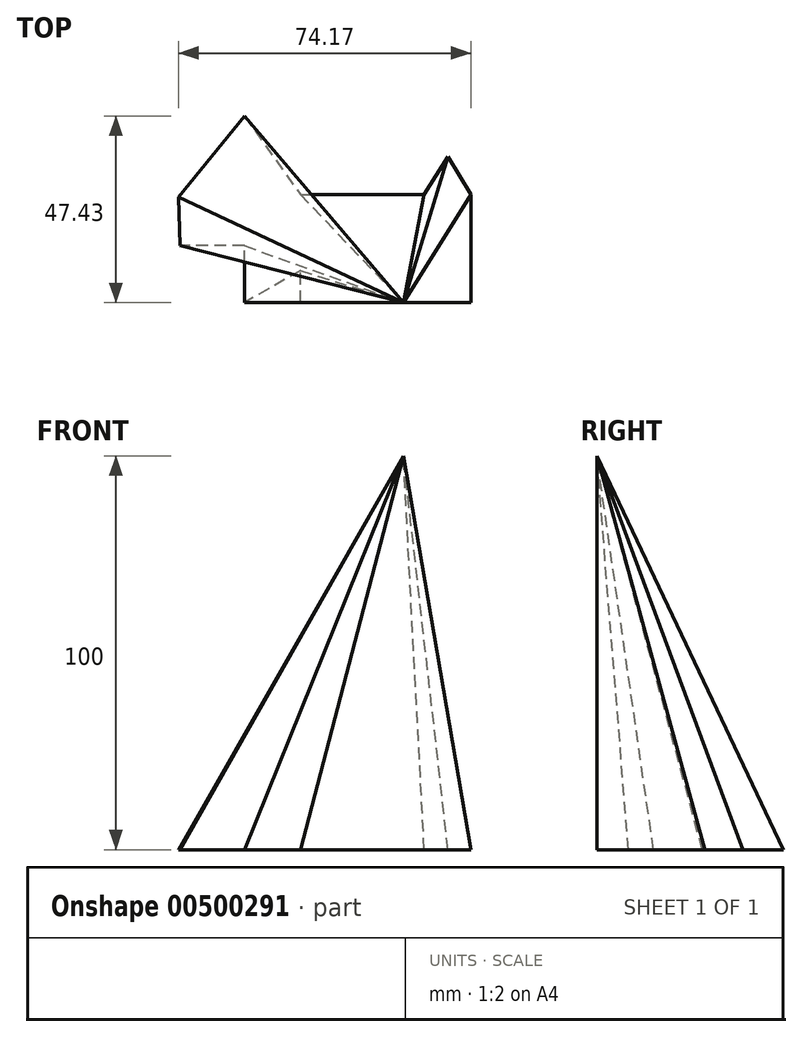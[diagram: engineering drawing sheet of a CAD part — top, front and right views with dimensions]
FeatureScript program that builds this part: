
annotation { "Feature Type Name" : "Feature", "Feature Type Description" : "" }
export const myFeature = defineFeature(function(context is Context, id is Id, definition is map)
    precondition{}
    {
        {
            var Q0;
            Q0=qCreatedBy(makeId("Top.planeOp"),FACE);
            var sketch = newSketch(context, id + "F0", { "sketchPlane" : qUnion([Q0])});
            skLineSegment(sketch, "E0", {"start": v(-57.04, 26.84) * mm, "end": v(-40.4, 47.43) * mm});
            skLineSegment(sketch, "E1", {"start": v(-40.4, 47.43) * mm, "end": v(-26.17, 27.45) * mm});
            skLineSegment(sketch, "E2", {"start": v(-26.17, 27.45) * mm, "end": v(5.32, 27.45) * mm});
            skLineSegment(sketch, "E3", {"start": v(5.32, 27.45) * mm, "end": v(11.37, 37.14) * mm});
            skLineSegment(sketch, "E4", {"start": v(11.37, 37.14) * mm, "end": v(17.13, 27.45) * mm});
            skLineSegment(sketch, "E5", {"start": v(17.13, 27.45) * mm, "end": v(17.13, 0) * mm});
            skLineSegment(sketch, "E6", {"start": v(17.13, 0) * mm, "end": v(-26.17, 0) * mm});
            skLineSegment(sketch, "E7", {"start": v(-26.17, 0) * mm, "end": v(-26.17, 8.07) * mm});
            skLineSegment(sketch, "E8", {"start": v(-26.17, 8.07) * mm, "end": v(-40.4, 0) * mm});
            skLineSegment(sketch, "E9", {"start": v(-40.4, 0) * mm, "end": v(-40.4, 14.43) * mm});
            skLineSegment(sketch, "E10", {"start": v(-40.4, 14.43) * mm, "end": v(-56.74, 14.43) * mm});
            skLineSegment(sketch, "E11", {"start": v(-56.74, 14.43) * mm, "end": v(-57.04, 26.84) * mm});
            skSolve(sketch);
        }
        {
            var Q0;
            Q0=qCreatedBy(makeId("Top.planeOp"),FACE);
            cPlane(context, id + "F1", {"entities" : qUnion([Q0]), "cplaneType" : CPlaneType.OFFSET, "offset" : 100 * mm, "width" : 152.4 * mm, "height" : 152.4 * mm});
        }
        {
            var Q0;
            Q0=qCreatedBy(id+"F1.planeOp",FACE);
            var sketch = newSketch(context, id + "F2", { "sketchPlane" : qUnion([Q0])});
            skPoint(sketch, "E12", {"position": v(0, 0) * mm});
            skSolve(sketch);
        }
        {
            var Q0;
            Q0=makeQuery(id+"F0.imprint","IMPRINT",FACE,{"disambiguationData":[TD([[makeQuery(id+"F0.imprint","IMPRINT",EDGE,{"derivedFrom":sQuery(id+"F0.wireOp",EDGE,"E0")}),-1.0]])]});
            var Q1;
            Q1=sQuery(id+"F2.wireOp",VERTEX,"E12");
            loft(context, id + "F3", {"sheetProfilesArray" : [{ "sheetProfileEntities" : qUnion([Q0]) }, { "sheetProfileEntities" : qUnion([Q1]) }]});
        }
    });
